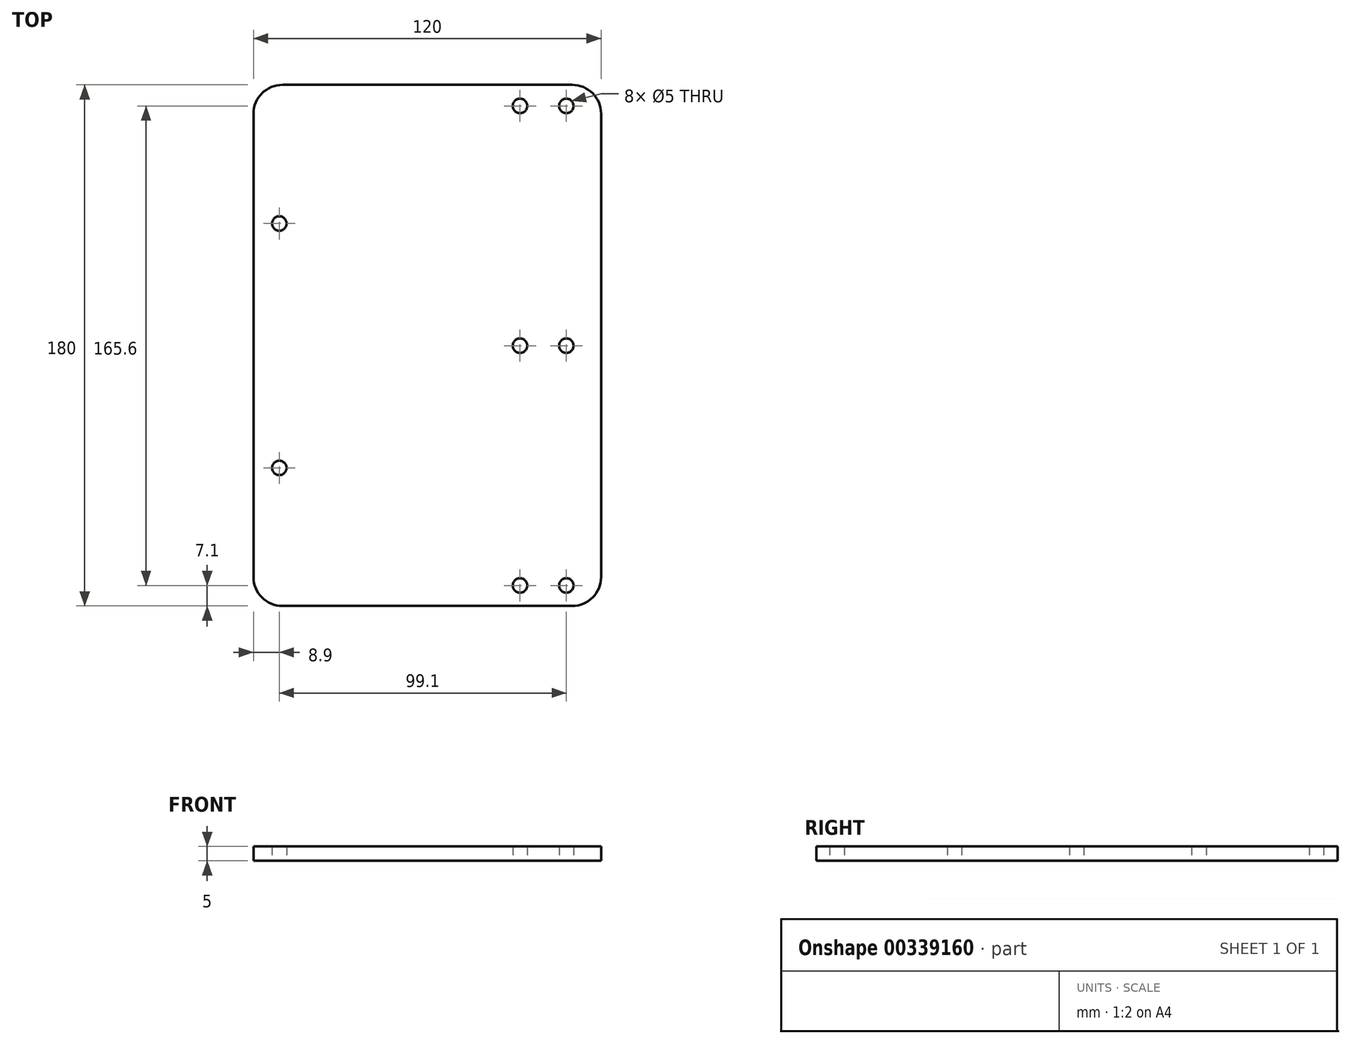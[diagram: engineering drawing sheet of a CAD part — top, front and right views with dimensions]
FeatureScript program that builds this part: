
annotation { "Feature Type Name" : "Feature", "Feature Type Description" : "" }
export const myFeature = defineFeature(function(context is Context, id is Id, definition is map)
    precondition{}
    {
        {
            var Q0;
            Q0=qCreatedBy(makeId("Top.planeOp"),FACE);
            var sketch = newSketch(context, id + "F0", { "sketchPlane" : qUnion([Q0])});
            skCircle(sketch, "E0", {"center": v(-8, 0) * mm, "radius": 2.5 * mm});
            skCircle(sketch, "E1", {"center": v(-8, -82.8) * mm, "radius": 2.5 * mm});
            skCircle(sketch, "E2", {"center": v(-8, 82.8) * mm, "radius": 2.5 * mm});
            skCircle(sketch, "E3", {"center": v(-91.1, 42.2) * mm, "radius": 2.5 * mm});
            skCircle(sketch, "E4", {"center": v(-91.1, -42.2) * mm, "radius": 2.5 * mm});
            skLineSegment(sketch, "E5", {"start": v(0, 0) * mm, "end": v(0, 40.5) * mm, "construction": true});
            skCircle(sketch, "E6.MirrorC", {"center": v(8, 82.8) * mm, "radius": 2.5 * mm});
            skCircle(sketch, "E7.MirrorC", {"center": v(8, 0) * mm, "radius": 2.5 * mm});
            skCircle(sketch, "E8.MirrorC", {"center": v(8, -82.8) * mm, "radius": 2.5 * mm});
            skLineSegment(sketch, "E9.bottom", {"start": v(-90, -89.9) * mm, "end": v(10, -89.9) * mm});
            skLineSegment(sketch, "E9.top", {"start": v(-90, 90.1) * mm, "end": v(10, 90.1) * mm});
            skLineSegment(sketch, "E9.left", {"start": v(-100, -79.9) * mm, "end": v(-100, 80.1) * mm});
            skPoint(sketch, "E9.middle", {"position": v(0, 0) * mm});
            skLineSegment(sketch, "E10", {"start": v(20, -79.9) * mm, "end": v(20, 80.1) * mm});
            skPoint(sketch, "E11.visualSharp", {"position": v(-100, -89.9) * mm});
            skArc(sketch, "E11.filletArc", {"start": v(-100, -79.9) * mm, "mid": v(-97.07, -86.97) * mm, "end": v(-90, -89.9) * mm});
            skPoint(sketch, "E12.visualSharp", {"position": v(-100, 90.1) * mm});
            skArc(sketch, "E12.filletArc", {"start": v(-90, 90.1) * mm, "mid": v(-97.07, 87.17) * mm, "end": v(-100, 80.1) * mm});
            skPoint(sketch, "E13.visualSharp", {"position": v(20, -89.9) * mm});
            skArc(sketch, "E13.filletArc", {"start": v(10, -89.9) * mm, "mid": v(17.07, -86.97) * mm, "end": v(20, -79.9) * mm});
            skPoint(sketch, "E14.visualSharp", {"position": v(20, 90.1) * mm});
            skArc(sketch, "E14.filletArc", {"start": v(20, 80.1) * mm, "mid": v(17.07, 87.17) * mm, "end": v(10, 90.1) * mm});
            skSolve(sketch);
        }
        {
            var Q0;
            Q0=makeQuery(id+"F0.imprint","IMPRINT",FACE,{"disambiguationData":[TD([[makeQuery(id+"F0.imprint","IMPRINT",EDGE,{"derivedFrom":sQuery(id+"F0.wireOp",EDGE,"E0")}),-1.0]])]});
            extrude(context, id + "F1", {"entities" : qUnion([Q0]), "depth" : 5 * mm});
        }
    });
